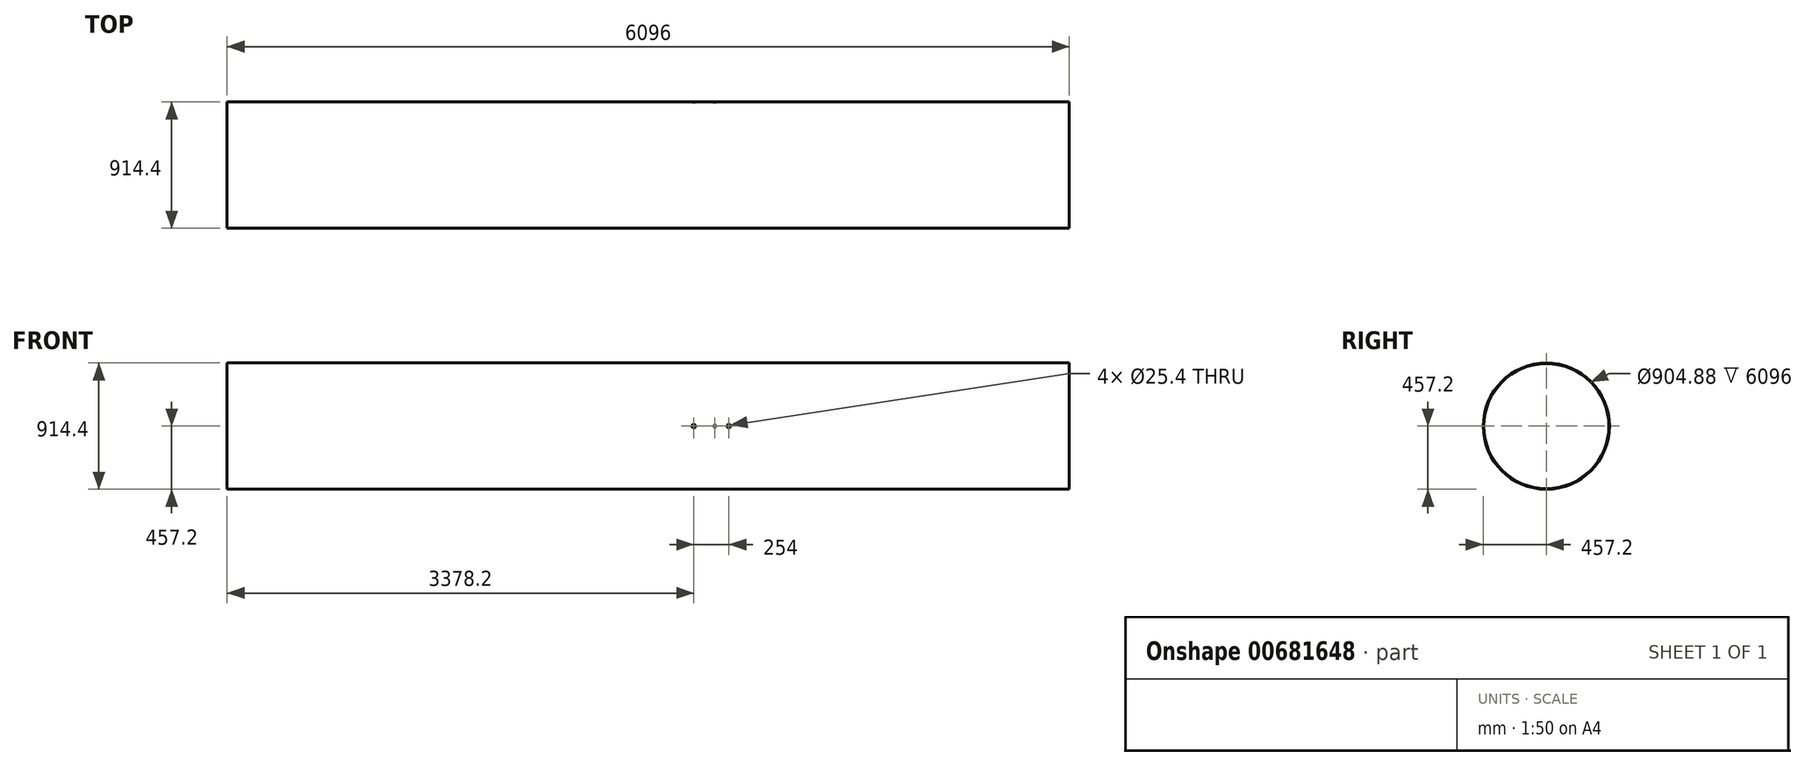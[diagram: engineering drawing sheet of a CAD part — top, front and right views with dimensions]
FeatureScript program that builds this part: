
annotation { "Feature Type Name" : "Feature", "Feature Type Description" : "" }
export const myFeature = defineFeature(function(context is Context, id is Id, definition is map)
    precondition{}
    {
        {
            var Q0;
            Q0=qCreatedBy(makeId("Right.planeOp"),FACE);
            var sketch = newSketch(context, id + "F0", { "sketchPlane" : qUnion([Q0])});
            skCircle(sketch, "E0", {"center": v(0, 0) * mm, "radius": 457.2 * mm});
            skCircle(sketch, "E1", {"center": v(0, 0) * mm, "radius": 452.44 * mm});
            skSolve(sketch);
        }
        {
            var Q0;
            Q0=makeQuery(id+"F0.imprint","IMPRINT",FACE,{"disambiguationData":[TD([[makeQuery(id+"F0.imprint","IMPRINT",EDGE,{"derivedFrom":sQuery(id+"F0.wireOp",EDGE,"E0")}),1.0]])]});
            extrude(context, id + "F1", {"entities" : qUnion([Q0]), "depth" : 6096 * mm, "offsetDistance" : 25.4 * mm});
        }
        {
            var Q0;
            Q0=qCreatedBy(makeId("Front.planeOp"),FACE);
            var sketch = newSketch(context, id + "F2", { "sketchPlane" : qUnion([Q0])});
            skLineSegment(sketch, "E2", {"start": v(0, 0) * mm, "end": v(3378.2, 0) * mm});
            skLineSegment(sketch, "E3", {"start": v(3378.2, 0) * mm, "end": v(3632.2, 0) * mm});
            skCircle(sketch, "E4", {"center": v(3378.2, 0) * mm, "radius": 12.7 * mm});
            skCircle(sketch, "E5", {"center": v(3632.2, 0) * mm, "radius": 12.7 * mm});
            skLineSegment(sketch, "E6", {"start": v(0, 0) * mm, "end": v(3530.6, 0) * mm});
            skCircle(sketch, "E7", {"center": v(3530.6, 0) * mm, "radius": 12.7 * mm});
            skSolve(sketch);
        }
        {
            var Q0;
            {var subQ0=sQuery(id+"F2.wireOp",EDGE,"E6");var subQ1=sQuery(id+"F2.wireOp",EDGE,"E4");var subQ2=makeQuery(id+"F2.imprint","INTERSECT",VERTEX,{"disambiguationData":[OD(0.0)],"derivedFrom":[subQ1,subQ0]});Q0=makeQuery(id+"F2.imprint","IMPRINT",FACE,{"disambiguationData":[TD([[makeQuery(id+"F2.imprint","IMPRINT",EDGE,{"disambiguationData":[TD([[subQ2,1.0]])],"derivedFrom":subQ1}),1.0]])]});}
            var Q1;
            {var subQ0=sQuery(id+"F2.wireOp",EDGE,"E6");var subQ1=sQuery(id+"F2.wireOp",EDGE,"E4");var subQ2=makeQuery(id+"F2.imprint","INTERSECT",VERTEX,{"disambiguationData":[OD(0.0)],"derivedFrom":[subQ1,subQ0]});Q1=makeQuery(id+"F2.imprint","IMPRINT",FACE,{"disambiguationData":[TD([[makeQuery(id+"F2.imprint","IMPRINT",EDGE,{"disambiguationData":[TD([[subQ2,-1.0]])],"derivedFrom":subQ1}),1.0]])]});}
            var Q2;
            Q2=makeQuery(id+"F2.imprint","IMPRINT",FACE,{"disambiguationData":[TD([[makeQuery(id+"F2.imprint","IMPRINT",EDGE,{"derivedFrom":sQuery(id+"F2.wireOp",EDGE,"E5")}),1.0]])]});
            extrude(context, id + "F3", {"entities" : qUnion([Q0, Q1, Q2]), "operationType" : NewBodyOperationType.REMOVE, "depth" : 998.22 * mm, "offsetDistance" : 25.4 * mm});
        }
        {
            var Q0;
            {var subQ0=sQuery(id+"F2.wireOp",EDGE,"E6");var subQ1=sQuery(id+"F2.wireOp",EDGE,"E3");var subQ2=makeQuery(id+"F2.imprint","INTERSECT",VERTEX,{"derivedFrom":[subQ1,subQ0]});Q0=makeQuery(id+"F2.imprint","IMPRINT",FACE,{"disambiguationData":[TD([[makeQuery(id+"F2.imprint","IMPRINT",EDGE,{"disambiguationData":[TD([[subQ2,-1.0]])],"derivedFrom":subQ1}),1.0]])]});}
            var Q1;
            {var subQ0=sQuery(id+"F2.wireOp",EDGE,"E6");var subQ1=sQuery(id+"F2.wireOp",EDGE,"E3");var subQ2=makeQuery(id+"F2.imprint","INTERSECT",VERTEX,{"derivedFrom":[subQ1,subQ0]});Q1=makeQuery(id+"F2.imprint","IMPRINT",FACE,{"disambiguationData":[TD([[makeQuery(id+"F2.imprint","IMPRINT",EDGE,{"disambiguationData":[TD([[subQ2,-1.0]])],"derivedFrom":subQ1}),-1.0]])]});}
            extrude(context, id + "F4", {"entities" : qUnion([Q0, Q1]), "operationType" : NewBodyOperationType.REMOVE, "oppositeDirection" : true, "depth" : 508 * mm, "offsetDistance" : 25.4 * mm});
        }
    });
